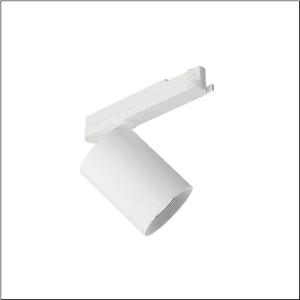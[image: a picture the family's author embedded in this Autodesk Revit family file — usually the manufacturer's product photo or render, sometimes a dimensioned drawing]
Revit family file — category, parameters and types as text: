
# Revit family: spot_21_51se13dbd5b
name_source: partatom
category: Lighting Fixtures
units: mm (PartAtom-declared; Revit-internal decimal feet)

## family parameters
Cut with Voids When Loaded = No
Host = Face
Light Source = No
Part Type = Normal
Room Calculation Point = No
Round Connector Dimension = Use Diameter
Shared = No

## types (1)
- --- (1 x LED, 5410 lm, 42.1 W, 4000K)
    Apparent Load = 42 VA
    CIE Flux Codes = 95 98 99 100 100
    Color Rendering = 90
    Color Temperature = 4000K
    Default Elevation = 1800 mm
    Description = Spot 21, directional spotlight, light control with lens, of PMMA, LED rated luminous flux: 5.200lm, light colour: 940, control gear: ECG Multilumen, with 3-phase adapter, mains connection: 220..240V, AC, 50/60Hz, of aluminium, traffic white (RAL 9016), length: 253mm, diameter: 105mm, protection rating (complete): IP20, insulation class (complete): insulation class I (protective earthing), certification: CE, impact resistance: IK02, permissible ambient temperature for indoor applications: -20..+40°C, packaging unit: 1 piece
    Height = 175 mm
    Lamp = 1 x LED
    Lamp Light Flux = 5410 lm
    Lamp Power = 42.1 W
    Lamp count = 1
    Length = 105 mm
    Luminous efficacy = 129 lm/W
    Manufacturer = Siteco
    ModVariant = No
    Model = 51SE13DBD5B
    Mounting Place = Ceiling
    Mounting Type = Pendant
    Number of Poles = 1
    OnlyDefault = Yes
    Power Factor = 1
    Product Name = Spot 21
    Product group = directional spotlight
    ProductGroupID = 905
    Protection Class = Protection class I
    Protection Degree = IP 20
    RLX_Detail_Level = 1
    RLX_Emergency_Light_Flux = 0 lm
    RLX_Emergency_Type = 0
    RLX_Emergency_Type_DB = No
    RlxData = <blob elided: 17705 chars, md5=efcd7f4b>
    Socket = socket
    Standby Power = 0 W
    System Light Flux = 5410 lm
    System Power = 42 W
    Type Comments = factory setting: luminous flux: 100 % | (ON | ON | ON | ON) | 1050 mA
    Type Image = l_1003976.jpg
    URL = http://relux.com
    VarID = @adj_075637
    Voltage = 0 V
    Weight = 0.00 kg
    Width = 0 mm  [stored 0 ft]

note: [stored X ft] marks values corroborated as IEEE doubles in the binary element streams (Revit-internal decimal feet)

## geometry (parser evidence)
native form markers: Blend x4, Sweep x10
no freeform markers — native parametric forms only
